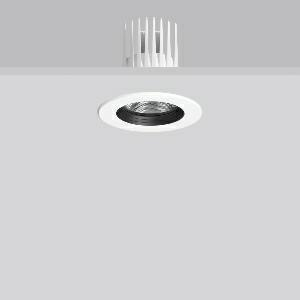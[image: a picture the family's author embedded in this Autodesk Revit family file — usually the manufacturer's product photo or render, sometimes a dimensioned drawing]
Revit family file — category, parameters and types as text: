
# Revit family: heledon_mini_e_901749_002_3_c2c2
name_source: partatom
category: Lighting Fixtures
units: mm (PartAtom-declared; Revit-internal decimal feet)

## family parameters
Cut with Voids When Loaded = No
Host = Face
Light Source = No
Part Type = Normal
Room Calculation Point = No
Round Connector Dimension = Use Diameter
Shared = No

## types (1)
- HELEDON mini E (1 x LED Modul 935, 3600 lm, 3500)
    Apparent Load = 29 VA
    Approval mark = CE
    CIE Flux Codes = 99 100 100 100 100
    Color Rendering = 92
    Color Temperature = 3500
    Default Elevation = 1800 mm
    Description = Series: HELEDON mini
Round recessed downlight. Housing: die-cast aluminium, powder-coated. Black plastic ring and recessed LED to prevent glare from the side. Optical assembly with reflector made of MIRO-Silver with 98% total light reflection for outstanding efficiency - can be changed without tools. Best colour rendering index Ra>90. Suitable for Recessed ceiling mounting. Installation without tools thanks to spring fastening system. Including separate LED converter with connecting cable 600 mm.High quality converter without flickering and stroboscopic effect. Through-wiring box (5 pole) available as accessory. The following accessories can be mounted without use of tools: interchangeable lenses, decorative glasses, honeycomb louvre, clear and frosted diffusers, white interchangeable plastic ring. 
Colour: traffic white, matt (RAL 9016)
Diameter: 124 mm
Height: 3 mm
Cut-out diameter: 114 mm
Recess height: 170 mm
Luminaire: recess height: 120 mm
Lamp: LED
Socket: without socket
Colour temperature: 3500K
Colour rendering index (CRI): 92
System power: 29 W
Rated luminous flux: 3600 lm
Luminous efficiency: 124 lm/W
Control gear: Regulated power supply
Protection class: II
Type of protection: IP 20
    Height = 0 mm  [stored 0 ft]
    Lamp = 1 x LED Modul 935
    Lamp Light Flux = 3600 lm
    Lamp count = 1
    Length = 124 mm  [stored 0.406824 ft]
    Lifetime = 50000 h
    Luminous efficacy = 124 lm/W
    Manufacturer = RZB
    ModVariant = No
    Model = 901749.002.3
    Mounting Place = Ceiling
    Mounting Type = Recessed
    Number of Poles = 1
    OnlyDefault = Yes
    Power Factor = 1
    Product Name = HELEDON mini E
    Product group = Recessed downlights
    ProductGroupID = 402
    Protection Class = Protection class II
    Protection Degree = IP 20
    RLX_Detail_Level = 1
    RLX_Emergency_Light_Flux = 0 lm
    RLX_Emergency_Type = 0
    RLX_Emergency_Type_DB = No
    RlxData = <blob elided: 126961 chars, md5=59088db4>
    Socket = socket
    Standby Power = 0 W
    System Light Flux = 3600 lm
    System Power = 29 W
    Type Comments = Product without accessories
    Type Image = 901657.002.jpg
    URL = http://relux.com
    VarID = ---
    Voltage = 230 V
    Voltage Range = 220-240 V
    Weight = 0.00 kg
    Width = 0 mm  [stored 0 ft]

note: [stored X ft] marks values corroborated as IEEE doubles in the binary element streams (Revit-internal decimal feet)

## geometry (parser evidence)
native form markers: Blend x4, Sweep x9
no freeform markers — native parametric forms only
